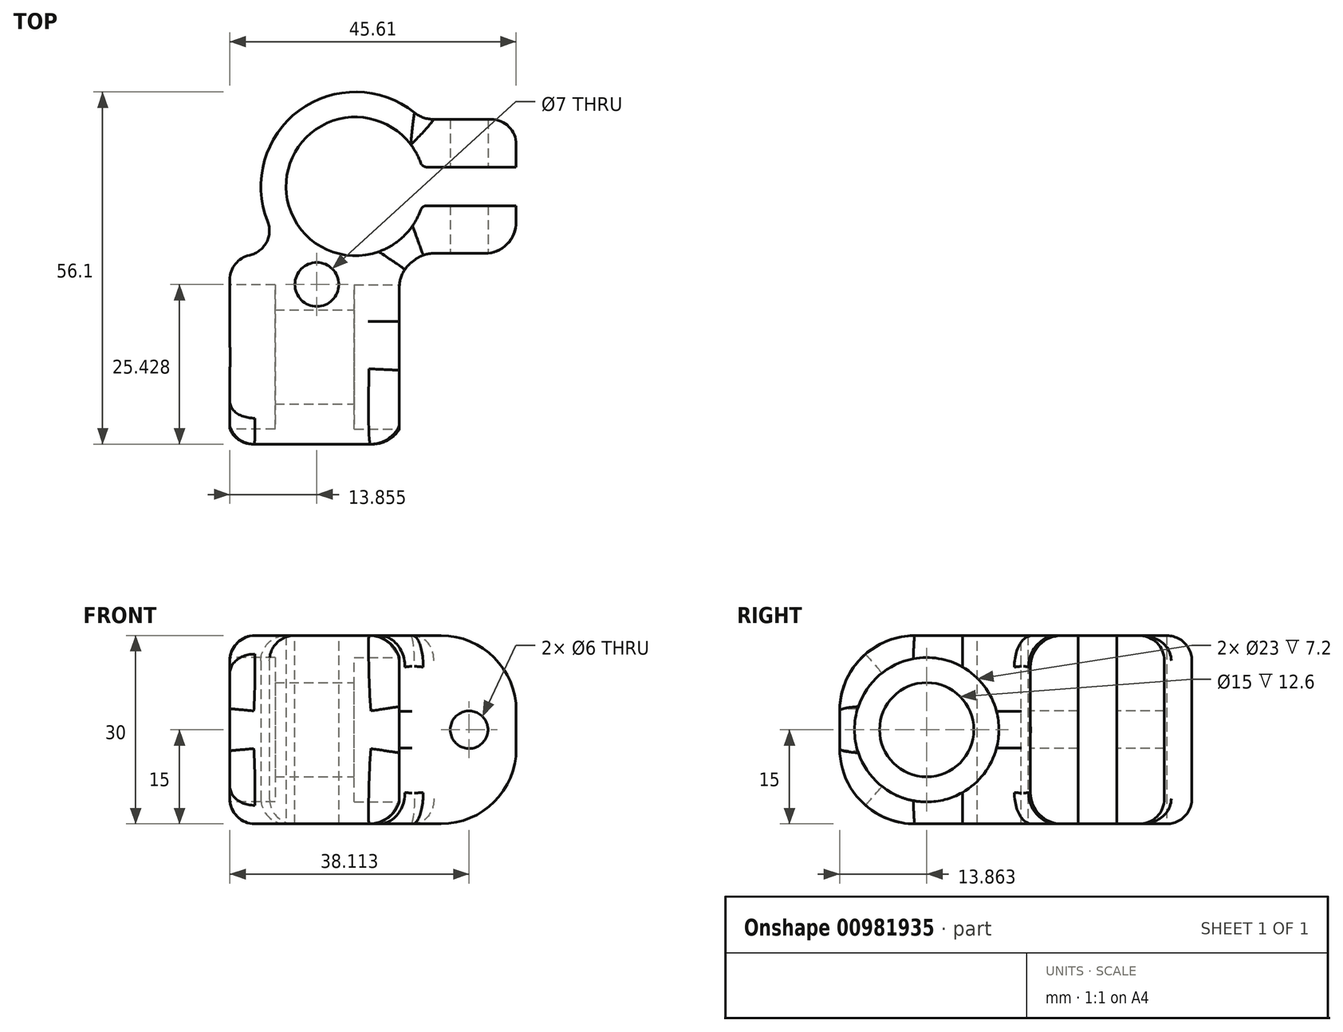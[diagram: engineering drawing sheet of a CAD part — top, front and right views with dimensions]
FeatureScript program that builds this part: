
annotation { "Feature Type Name" : "Feature", "Feature Type Description" : "" }
export const myFeature = defineFeature(function(context is Context, id is Id, definition is map)
    precondition{}
    {
        {
            var Q0;
            Q0=qCreatedBy(makeId("Top.planeOp"),FACE);
            var sketch = newSketch(context, id + "F0", { "sketchPlane" : qUnion([Q0])});
            skArc(sketch, "E0", {"start": v(10.61, 3.08) * mm, "mid": v(-11.05, 0) * mm, "end": v(10.61, -3.08) * mm});
            skArc(sketch, "E1", {"start": v(10.61, 10.67) * mm, "mid": v(-10.86, 10.42) * mm, "end": v(-10.22, -11.05) * mm});
            skLineSegment(sketch, "E2.bottom", {"start": v(0, -41.05) * mm, "end": v(-20, -41.05) * mm});
            skLineSegment(sketch, "E2.top", {"start": v(-10.22, -11.05) * mm, "end": v(-20, -11.05) * mm});
            skLineSegment(sketch, "E2.right", {"start": v(-20, -41.05) * mm, "end": v(-20, -11.05) * mm});
            skLineSegment(sketch, "E3.bottom", {"start": v(0, -41.05) * mm, "end": v(7, -41.05) * mm});
            skLineSegment(sketch, "E3.right", {"start": v(7, -41.05) * mm, "end": v(7, -13.32) * mm});
            skLineSegment(sketch, "E4.bottom", {"start": v(25.61, 3.08) * mm, "end": v(10.61, 3.08) * mm});
            skLineSegment(sketch, "E4.top", {"start": v(25.61, 10.67) * mm, "end": v(10.61, 10.67) * mm});
            skLineSegment(sketch, "E4.left", {"start": v(25.61, 3.08) * mm, "end": v(25.61, 10.67) * mm});
            skLineSegment(sketch, "E5.MirrorCS", {"start": v(25.61, -10.67) * mm, "end": v(10.61, -10.67) * mm});
            skLineSegment(sketch, "E6.MirrorCS", {"start": v(25.61, -3.08) * mm, "end": v(10.61, -3.08) * mm});
            skLineSegment(sketch, "E7.MirrorCS", {"start": v(25.61, -3.08) * mm, "end": v(25.61, -10.67) * mm});
            skPoint(sketch, "E8.MirrorCS.end.orphan", {"position": v(10.61, -10.67) * mm});
            skPoint(sketch, "E8.MirrorCS.start.orphan", {"position": v(10.61, -3.08) * mm});
            skPoint(sketch, "E3.top.end.orphan", {"position": v(7, -11.05) * mm});
            skArc(sketch, "E9.trimOffspring", {"start": v(7, -13.32) * mm, "mid": v(8.9, -12.13) * mm, "end": v(10.61, -10.67) * mm});
            skSolve(sketch);
        }
        {
            var Q0;
            Q0=makeQuery(id+"F0.imprint","IMPRINT",FACE,{"disambiguationData":[TD([[makeQuery(id+"F0.imprint","IMPRINT",EDGE,{"derivedFrom":sQuery(id+"F0.wireOp",EDGE,"E0")}),-1.0]])]});
            extrude(context, id + "F1", {"entities" : qUnion([Q0]), "depth" : 30 * mm, "offsetDistance" : 25 * mm});
        }
        {
            var Q0;
            Q0=makeQuery(id+"F1.opExtrude","SWEPT_FACE",FACE,{"disambiguationData":[OSD([sQuery(id+"F0.wireOp",EDGE,"E3.right")])]});
            var sketch = newSketch(context, id + "F2", { "sketchPlane" : qUnion([Q0])});
            skLineSegment(sketch, "E10", {"start": v(-41.05, 15) * mm, "end": v(-13.32, 15) * mm, "construction": true});
            skLineSegment(sketch, "E11", {"start": v(-27.19, 30) * mm, "end": v(-27.19, 0) * mm, "construction": true});
            skPoint(sketch, "E12", {"position": v(-27.19, 15) * mm});
            skCircle(sketch, "E13", {"center": v(-27.19, 15) * mm, "radius": 7.5 * mm});
            skCircle(sketch, "E14", {"center": v(-27.19, 15) * mm, "radius": 11.5 * mm});
            skSolve(sketch);
        }
        {
            var Q0;
            Q0=makeQuery(id+"F2.imprint","IMPRINT",FACE,{"disambiguationData":[TD([[makeQuery(id+"F2.imprint","IMPRINT",EDGE,{"derivedFrom":sQuery(id+"F2.wireOp",EDGE,"E13")}),1.0]])]});
            var Q1;
            Q1=makeQuery(id+"F1.opExtrude","SWEPT_FACE",FACE,{"disambiguationData":[OSD([sQuery(id+"F0.wireOp",EDGE,"E2.right")])]});
            extrude(context, id + "F3", {"entities" : qUnion([Q0]), "operationType" : NewBodyOperationType.REMOVE, "endBound" : BoundingType.UP_TO_SURFACE, "oppositeDirection" : true, "depth" : 25 * mm, "endBoundEntityFace" : qUnion([Q1]), "offsetDistance" : 25 * mm});
        }
        {
            var Q0;
            Q0=makeQuery(id+"F2.imprint","IMPRINT",FACE,{"disambiguationData":[TD([[makeQuery(id+"F2.imprint","IMPRINT",EDGE,{"derivedFrom":sQuery(id+"F2.wireOp",EDGE,"E13")}),-1.0]])]});
            extrude(context, id + "F4", {"entities" : qUnion([Q0]), "operationType" : NewBodyOperationType.REMOVE, "oppositeDirection" : true, "depth" : 7.2 * mm, "offsetDistance" : 25 * mm});
        }
        {
            var Q0;
            Q0=makeQuery(id+"F1.opExtrude","SWEPT_FACE",FACE,{"disambiguationData":[OSD([sQuery(id+"F0.wireOp",EDGE,"E2.right")])]});
            var sketch = newSketch(context, id + "F5", { "sketchPlane" : qUnion([Q0])});
            skCircle(sketch, "E15", {"center": v(27.19, 15) * mm, "radius": 11.5 * mm});
            skCircle(sketch, "E16", {"center": v(27.19, 15) * mm, "radius": 7.5 * mm});
            skSolve(sketch);
        }
        {
            var Q0;
            Q0=makeQuery(id+"F5.imprint","IMPRINT",FACE,{"disambiguationData":[TD([[makeQuery(id+"F5.imprint","IMPRINT",EDGE,{"derivedFrom":sQuery(id+"F5.wireOp",EDGE,"E15")}),1.0]])]});
            extrude(context, id + "F6", {"entities" : qUnion([Q0]), "operationType" : NewBodyOperationType.REMOVE, "oppositeDirection" : true, "depth" : 7.2 * mm, "offsetDistance" : 25 * mm});
        }
        {
            var Q0;
            Q0=makeQuery(id+"F1.opExtrude","SWEPT_FACE",FACE,{"disambiguationData":[OSD([sQuery(id+"F0.wireOp",EDGE,"E5.MirrorCS")])]});
            var sketch = newSketch(context, id + "F7", { "sketchPlane" : qUnion([Q0])});
            skLineSegment(sketch, "E17", {"start": v(18.11, 30) * mm, "end": v(18.11, 5.09) * mm, "construction": true});
            skLineSegment(sketch, "E18", {"start": v(25.61, 15) * mm, "end": v(13.55, 15) * mm, "construction": true});
            skPoint(sketch, "E19", {"position": v(18.11, 15) * mm});
            skCircle(sketch, "E20", {"center": v(18.11, 15) * mm, "radius": 3 * mm});
            skSolve(sketch);
        }
        {
            var Q0;
            Q0=makeQuery(id+"F7.imprint","IMPRINT",FACE,{"disambiguationData":[TD([[makeQuery(id+"F7.imprint","IMPRINT",EDGE,{"derivedFrom":sQuery(id+"F7.wireOp",EDGE,"E20")}),1.0]])]});
            var Q1;
            Q1=makeQuery(id+"F1.opExtrude","SWEPT_FACE",FACE,{"disambiguationData":[OSD([sQuery(id+"F0.wireOp",EDGE,"E4.top")])]});
            extrude(context, id + "F8", {"entities" : qUnion([Q0]), "operationType" : NewBodyOperationType.REMOVE, "endBound" : BoundingType.UP_TO_SURFACE, "oppositeDirection" : true, "depth" : 25 * mm, "endBoundEntityFace" : qUnion([Q1]), "offsetDistance" : 25 * mm});
        }
        {
            var Q0;
            Q0=makeQuery(id+"F1.opExtrude","CAP_EDGE",EDGE,{"disambiguationData":[OSD([sQuery(id+"F0.wireOp",EDGE,"E7.MirrorCS")])],"isStart":false});
            var Q1;
            Q1=makeQuery(id+"F1.opExtrude","CAP_EDGE",EDGE,{"disambiguationData":[OSD([sQuery(id+"F0.wireOp",EDGE,"E4.left")])],"isStart":false});
            var Q2;
            Q2=makeQuery(id+"F1.opExtrude","CAP_EDGE",EDGE,{"disambiguationData":[OSD([sQuery(id+"F0.wireOp",EDGE,"E7.MirrorCS")])],"isStart":true});
            var Q3;
            Q3=makeQuery(id+"F1.opExtrude","CAP_EDGE",EDGE,{"disambiguationData":[OSD([sQuery(id+"F0.wireOp",EDGE,"E4.left")])],"isStart":true});
            fillet(context, id + "F9", {"entities" : qUnion([Q0, Q1, Q2, Q3]), "radius" : 12 * mm, "tangentPropagation" : true, "allowEdgeOverflow" : false});
        }
        {
            var Q0;
            Q0=makeQuery(id+"F1.opExtrude","SWEPT_EDGE",EDGE,{"disambiguationData":[OSD([sQuery(id+"F0.wireOp",EDGE,"E5.MirrorCS"),sQuery(id+"F0.wireOp",EDGE,"E9.trimOffspring")])]});
            var Q1;
            Q1=makeQuery(id+"F1.opExtrude","SWEPT_EDGE",EDGE,{"disambiguationData":[OSD([sQuery(id+"F0.wireOp",EDGE,"E3.right"),sQuery(id+"F0.wireOp",EDGE,"E9.trimOffspring")])]});
            fillet(context, id + "F10", {"entities" : qUnion([Q0, Q1]), "radius" : 5 * mm, "tangentPropagation" : true, "allowEdgeOverflow" : false});
        }
        {
            var Q0;
            Q0=makeQuery(id+"F1.opExtrude","CAP_EDGE",EDGE,{"disambiguationData":[OSD([sQuery(id+"F0.wireOp",EDGE,"E2.bottom"),sQuery(id+"F0.wireOp",EDGE,"E3.bottom")])],"isStart":false});
            var Q1;
            Q1=makeQuery(id+"F1.opExtrude","CAP_EDGE",EDGE,{"disambiguationData":[OSD([sQuery(id+"F0.wireOp",EDGE,"E2.bottom"),sQuery(id+"F0.wireOp",EDGE,"E3.bottom")])],"isStart":true});
            fillet(context, id + "F11", {"entities" : qUnion([Q0, Q1]), "radius" : 12 * mm, "tangentPropagation" : true, "allowEdgeOverflow" : false});
        }
        {
            var Q0;
            Q0=makeQuery(id+"F1.opExtrude","CAP_EDGE",EDGE,{"disambiguationData":[OSD([sQuery(id+"F0.wireOp",EDGE,"E2.right")])],"isStart":false});
            var Q1;
            Q1=makeQuery(id+"F1.opExtrude","CAP_EDGE",EDGE,{"disambiguationData":[OSD([sQuery(id+"F0.wireOp",EDGE,"E2.right")])],"isStart":true});
            var Q2;
            Q2=makeQuery(id+"F11.opFillet","BLEND_EDGE",EDGE,{"blendedFrom":[makeQuery(id+"F1.opExtrude","CAP_EDGE",EDGE,{"disambiguationData":[OSD([sQuery(id+"F0.wireOp",EDGE,"E2.bottom"),sQuery(id+"F0.wireOp",EDGE,"E3.bottom")])],"isStart":true}),makeQuery(id+"F1.opExtrude","SWEPT_FACE",FACE,{"disambiguationData":[OSD([sQuery(id+"F0.wireOp",EDGE,"E2.right")])]})],"blendedInto":[makeQuery(id+"F1.opExtrude","SWEPT_FACE",FACE,{"disambiguationData":[OSD([sQuery(id+"F0.wireOp",EDGE,"E2.right")])]})]});
            var Q3;
            Q3=makeQuery(id+"F1.opExtrude","SWEPT_EDGE",EDGE,{"disambiguationData":[OSD([sQuery(id+"F0.wireOp",EDGE,"E2.bottom"),sQuery(id+"F0.wireOp",EDGE,"E2.right")])]});
            var Q4;
            Q4=makeQuery(id+"F11.opFillet","BLEND_EDGE",EDGE,{"blendedFrom":[makeQuery(id+"F1.opExtrude","CAP_EDGE",EDGE,{"disambiguationData":[OSD([sQuery(id+"F0.wireOp",EDGE,"E2.bottom"),sQuery(id+"F0.wireOp",EDGE,"E3.bottom")])],"isStart":false}),makeQuery(id+"F1.opExtrude","SWEPT_FACE",FACE,{"disambiguationData":[OSD([sQuery(id+"F0.wireOp",EDGE,"E2.right")])]})],"blendedInto":[makeQuery(id+"F1.opExtrude","SWEPT_FACE",FACE,{"disambiguationData":[OSD([sQuery(id+"F0.wireOp",EDGE,"E2.right")])]})]});
            fillet(context, id + "F12", {"entities" : qUnion([Q0, Q1, Q2, Q3, Q4]), "radius" : 4 * mm, "tangentPropagation" : true, "allowEdgeOverflow" : false});
        }
        {
            var Q0;
            Q0=makeQuery(id+"F11.opFillet","BLEND_EDGE",EDGE,{"blendedFrom":[makeQuery(id+"F1.opExtrude","CAP_EDGE",EDGE,{"disambiguationData":[OSD([sQuery(id+"F0.wireOp",EDGE,"E2.bottom"),sQuery(id+"F0.wireOp",EDGE,"E3.bottom")])],"isStart":false}),makeQuery(id+"F1.opExtrude","SWEPT_FACE",FACE,{"disambiguationData":[OSD([sQuery(id+"F0.wireOp",EDGE,"E3.right")])]})],"blendedInto":[makeQuery(id+"F1.opExtrude","SWEPT_FACE",FACE,{"disambiguationData":[OSD([sQuery(id+"F0.wireOp",EDGE,"E3.right")])]})]});
            var Q1;
            Q1=makeQuery(id+"F1.opExtrude","SWEPT_EDGE",EDGE,{"disambiguationData":[OSD([sQuery(id+"F0.wireOp",EDGE,"E3.bottom"),sQuery(id+"F0.wireOp",EDGE,"E3.right")])]});
            var Q2;
            Q2=makeQuery(id+"F11.opFillet","BLEND_EDGE",EDGE,{"blendedFrom":[makeQuery(id+"F1.opExtrude","CAP_EDGE",EDGE,{"disambiguationData":[OSD([sQuery(id+"F0.wireOp",EDGE,"E2.bottom"),sQuery(id+"F0.wireOp",EDGE,"E3.bottom")])],"isStart":true}),makeQuery(id+"F1.opExtrude","SWEPT_FACE",FACE,{"disambiguationData":[OSD([sQuery(id+"F0.wireOp",EDGE,"E3.right")])]})],"blendedInto":[makeQuery(id+"F1.opExtrude","SWEPT_FACE",FACE,{"disambiguationData":[OSD([sQuery(id+"F0.wireOp",EDGE,"E3.right")])]})]});
            fillet(context, id + "F13", {"entities" : qUnion([Q0, Q1, Q2]), "radius" : 5 * mm, "tangentPropagation" : true, "allowEdgeOverflow" : false});
        }
        {
            var Q0;
            Q0=makeQuery(id+"F1.opExtrude","SWEPT_EDGE",EDGE,{"disambiguationData":[OSD([sQuery(id+"F0.wireOp",EDGE,"E1"),sQuery(id+"F0.wireOp",EDGE,"E2.top")])]});
            fillet(context, id + "F14", {"entities" : qUnion([Q0]), "radius" : 4 * mm, "tangentPropagation" : true, "allowEdgeOverflow" : false});
        }
        {
            var Q0;
            Q0=makeQuery(id+"F1.opExtrude","SWEPT_EDGE",EDGE,{"disambiguationData":[OSD([sQuery(id+"F0.wireOp",EDGE,"E2.top"),sQuery(id+"F0.wireOp",EDGE,"E2.right")])]});
            fillet(context, id + "F15", {"entities" : qUnion([Q0]), "radius" : 4 * mm, "tangentPropagation" : true, "allowEdgeOverflow" : false});
        }
        {
            var Q0;
            Q0=makeQuery(id+"F9.opFillet","BLEND_EDGE",EDGE,{"blendedFrom":[makeQuery(id+"F1.opExtrude","CAP_EDGE",EDGE,{"disambiguationData":[OSD([sQuery(id+"F0.wireOp",EDGE,"E4.left")])],"isStart":false}),makeQuery(id+"F1.opExtrude","SWEPT_FACE",FACE,{"disambiguationData":[OSD([sQuery(id+"F0.wireOp",EDGE,"E4.top")])]})],"blendedInto":[makeQuery(id+"F1.opExtrude","SWEPT_FACE",FACE,{"disambiguationData":[OSD([sQuery(id+"F0.wireOp",EDGE,"E4.top")])]})]});
            var Q1;
            Q1=makeQuery(id+"F1.opExtrude","SWEPT_EDGE",EDGE,{"disambiguationData":[OSD([sQuery(id+"F0.wireOp",EDGE,"E4.top"),sQuery(id+"F0.wireOp",EDGE,"E4.left")])]});
            var Q2;
            Q2=makeQuery(id+"F9.opFillet","BLEND_EDGE",EDGE,{"blendedFrom":[makeQuery(id+"F1.opExtrude","CAP_EDGE",EDGE,{"disambiguationData":[OSD([sQuery(id+"F0.wireOp",EDGE,"E4.left")])],"isStart":true}),makeQuery(id+"F1.opExtrude","SWEPT_FACE",FACE,{"disambiguationData":[OSD([sQuery(id+"F0.wireOp",EDGE,"E4.top")])]})],"blendedInto":[makeQuery(id+"F1.opExtrude","SWEPT_FACE",FACE,{"disambiguationData":[OSD([sQuery(id+"F0.wireOp",EDGE,"E4.top")])]})]});
            fillet(context, id + "F16", {"entities" : qUnion([Q0, Q1, Q2]), "radius" : 4 * mm, "tangentPropagation" : true, "allowEdgeOverflow" : false});
        }
        {
            var Q0;
            Q0=makeQuery(id+"F1.opExtrude","SWEPT_EDGE",EDGE,{"disambiguationData":[OSD([sQuery(id+"F0.wireOp",EDGE,"E0"),sQuery(id+"F0.wireOp",EDGE,"E4.bottom")])]});
            var Q1;
            Q1=makeQuery(id+"F1.opExtrude","SWEPT_EDGE",EDGE,{"disambiguationData":[OSD([sQuery(id+"F0.wireOp",EDGE,"E0"),sQuery(id+"F0.wireOp",EDGE,"E6.MirrorCS")])]});
            fillet(context, id + "F17", {"entities" : qUnion([Q0, Q1]), "radius" : 1 * mm, "tangentPropagation" : true, "allowEdgeOverflow" : false});
        }
        {
            var Q0;
            Q0=makeQuery(id+"F1.opExtrude","SWEPT_EDGE",EDGE,{"disambiguationData":[OSD([sQuery(id+"F0.wireOp",EDGE,"E1"),sQuery(id+"F0.wireOp",EDGE,"E4.top")])]});
            fillet(context, id + "F18", {"entities" : qUnion([Q0]), "radius" : 5 * mm, "tangentPropagation" : true, "allowEdgeOverflow" : false});
        }
        {
            var Q0;
            Q0=makeQuery(id+"F15.opFillet","SPLIT",FACE,{"disambiguationData":[OD(1.0)],"derivedFrom":makeQuery(id+"F13.opFillet","SPLIT",FACE,{"disambiguationData":[OD(1.0)],"derivedFrom":makeQuery(id+"F1.opExtrude","CAP_FACE",FACE,{"disambiguationData":[OSD([sQuery(id+"F0.wireOp",EDGE,"E0"),sQuery(id+"F0.wireOp",EDGE,"E1"),sQuery(id+"F0.wireOp",EDGE,"E2.bottom"),sQuery(id+"F0.wireOp",EDGE,"E2.top"),sQuery(id+"F0.wireOp",EDGE,"E2.right"),sQuery(id+"F0.wireOp",EDGE,"E3.bottom"),sQuery(id+"F0.wireOp",EDGE,"E3.right"),sQuery(id+"F0.wireOp",EDGE,"E4.bottom"),sQuery(id+"F0.wireOp",EDGE,"E4.top"),sQuery(id+"F0.wireOp",EDGE,"E4.left"),sQuery(id+"F0.wireOp",EDGE,"E5.MirrorCS"),sQuery(id+"F0.wireOp",EDGE,"E6.MirrorCS"),sQuery(id+"F0.wireOp",EDGE,"E7.MirrorCS"),sQuery(id+"F0.wireOp",EDGE,"E9.trimOffspring")])],"isStart":false})})});
            var sketch = newSketch(context, id + "F19", { "sketchPlane" : qUnion([Q0])});
            skPoint(sketch, "E21", {"position": v(-6.14, -15.62) * mm});
            skCircle(sketch, "E22", {"center": v(-6.14, -15.62) * mm, "radius": 3.5 * mm});
            skSolve(sketch);
        }
        {
            var Q0;
            Q0=makeQuery(id+"F19.imprint","IMPRINT",FACE,{"disambiguationData":[TD([[makeQuery(id+"F19.imprint","IMPRINT",EDGE,{"derivedFrom":sQuery(id+"F19.wireOp",EDGE,"E22")}),1.0]])]});
            var Q1;
            Q1=makeQuery(id+"F15.opFillet","SPLIT",FACE,{"disambiguationData":[OD(1.0)],"derivedFrom":makeQuery(id+"F13.opFillet","SPLIT",FACE,{"disambiguationData":[OD(1.0)],"derivedFrom":makeQuery(id+"F1.opExtrude","CAP_FACE",FACE,{"disambiguationData":[OSD([sQuery(id+"F0.wireOp",EDGE,"E0"),sQuery(id+"F0.wireOp",EDGE,"E1"),sQuery(id+"F0.wireOp",EDGE,"E2.bottom"),sQuery(id+"F0.wireOp",EDGE,"E2.top"),sQuery(id+"F0.wireOp",EDGE,"E2.right"),sQuery(id+"F0.wireOp",EDGE,"E3.bottom"),sQuery(id+"F0.wireOp",EDGE,"E3.right"),sQuery(id+"F0.wireOp",EDGE,"E4.bottom"),sQuery(id+"F0.wireOp",EDGE,"E4.top"),sQuery(id+"F0.wireOp",EDGE,"E4.left"),sQuery(id+"F0.wireOp",EDGE,"E5.MirrorCS"),sQuery(id+"F0.wireOp",EDGE,"E6.MirrorCS"),sQuery(id+"F0.wireOp",EDGE,"E7.MirrorCS"),sQuery(id+"F0.wireOp",EDGE,"E9.trimOffspring")])],"isStart":true})})});
            extrude(context, id + "F20", {"entities" : qUnion([Q0]), "operationType" : NewBodyOperationType.REMOVE, "endBound" : BoundingType.UP_TO_SURFACE, "oppositeDirection" : true, "depth" : 25 * mm, "endBoundEntityFace" : qUnion([Q1]), "offsetDistance" : 25 * mm});
        }
        {
            var Q0;
            Q0=makeQuery(id+"F19.imprint","IMPRINT",FACE,{"disambiguationData":[TD([[makeQuery(id+"F19.imprint","IMPRINT",EDGE,{"derivedFrom":sQuery(id+"F19.wireOp",EDGE,"E22")}),1.0]])]});
            extrude(context, id + "F21", {"entities" : qUnion([Q0]), "operationType" : NewBodyOperationType.REMOVE, "oppositeDirection" : true, "depth" : 25 * mm, "offsetDistance" : 25 * mm});
        }
    });
